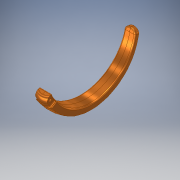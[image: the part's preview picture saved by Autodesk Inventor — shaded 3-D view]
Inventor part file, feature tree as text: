
AUTODESK INVENTOR PART (.ipt)
format: ipt  version: 2019 (Build 230136000, 136)  size: 1,146,368 bytes
history: native  units: mm
features: fillet x4, other x4, direct_edit x4, plane x2, move_body x2
ambient origin geometry x8: Origin, YZ Plane, XZ Plane, XY Plane, X Axis, Y Axis, Z Axis, Center Point
bodies: Volumenkörper1 (feature_tree), Volumenkörper3 (feature_tree), Volumenkörper2 (feature_tree), Volumenkörper4 (feature_tree)
feature tree (16):
  fillet  "Rundung1"  Radius=0.4mm
  plane  "Arbeitsebene1"
  other  "Trennen1"
  direct_edit  "Direktbearbeitung2"
  direct_edit  "Direktbearbeitung6"
  direct_edit  "Direktbearbeitung7"
  direct_edit  "Direktbearbeitung8"
  plane  "Arbeitsebene3"
  fillet  "Rundung2"  Radius=10.769mm
  other  "Kombinieren1"
  fillet  "Rundung3"  Radius=15.0mm
  fillet  "Rundung4"  [1 undecoded]
  other  "Skalierung2"
  other  "Skalierung3"
  move_body  "Verschieben4"
  move_body  "Verschieben5"
note: 1 required parameter value undecoded (feature->parameter linkage not recoverable at this tier; creation-order binding heuristic only, values carry confidence <= 0.55)
